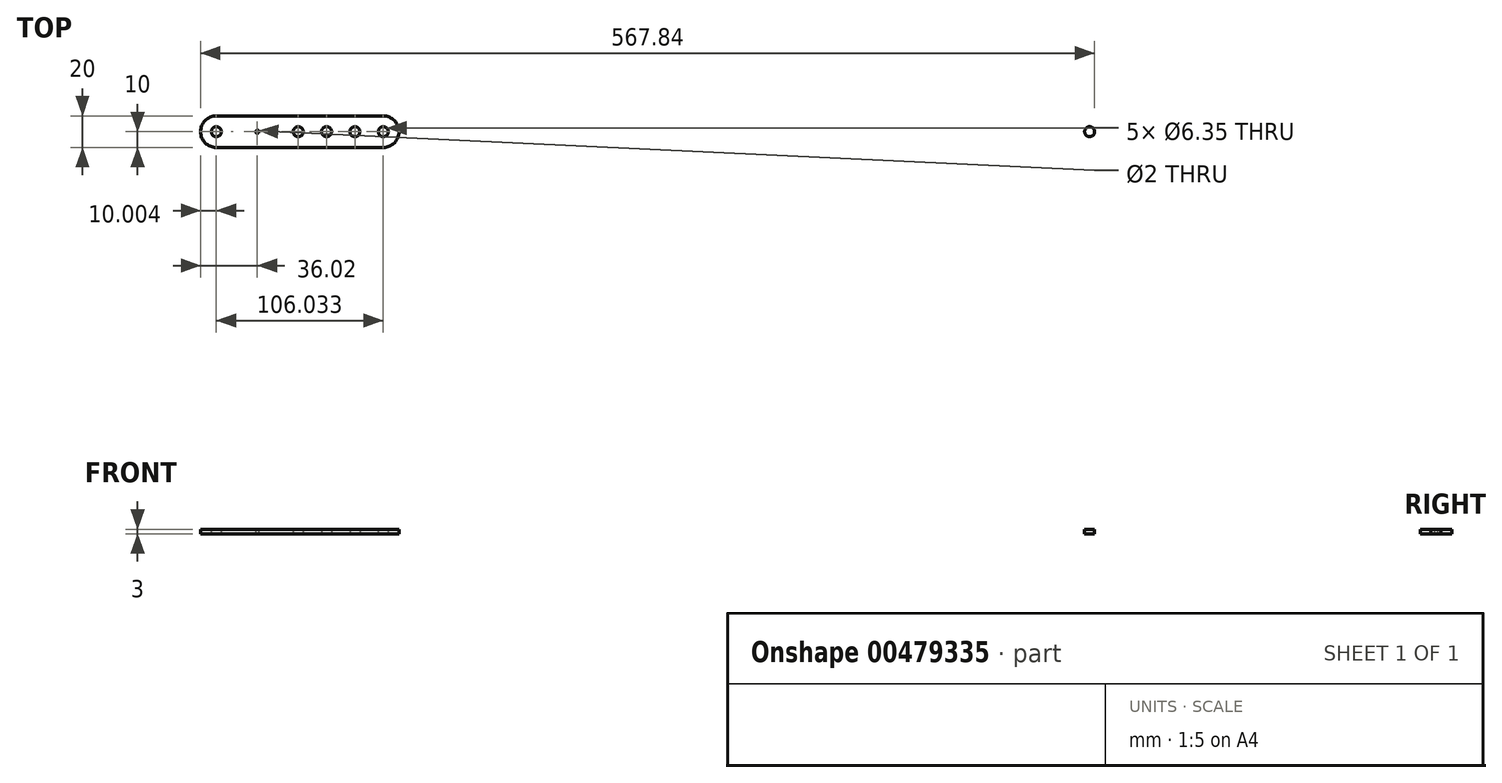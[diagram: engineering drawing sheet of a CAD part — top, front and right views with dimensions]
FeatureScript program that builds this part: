
annotation { "Feature Type Name" : "Feature", "Feature Type Description" : "" }
export const myFeature = defineFeature(function(context is Context, id is Id, definition is map)
    precondition{}
    {
        {
            var Q0;
            Q0=qCreatedBy(makeId("Top.planeOp"),FACE);
            var sketch = newSketch(context, id + "F0", { "sketchPlane" : qUnion([Q0])});
            skLineSegment(sketch, "E0", {"start": v(0, 0) * mm, "end": v(2599.19, 0) * mm, "construction": true});
            skCircle(sketch, "E1", {"center": v(528.65, 0) * mm, "radius": 3.18 * mm});
            skCircle(sketch, "E2", {"center": v(26.02, 0) * mm, "radius": 3.18 * mm});
            skCircle(sketch, "E3", {"center": v(0, 0) * mm, "radius": 13.8 * mm, "construction": true});
            skCircle(sketch, "E4.cCircle", {"center": v(26.02, 0) * mm, "radius": 6.35 * mm, "construction": true});
            skLineSegment(sketch, "E4.0", {"start": v(32.37, 0) * mm, "end": v(29.2, -5.5) * mm, "construction": true});
            skLineSegment(sketch, "E4.1", {"start": v(29.2, -5.5) * mm, "end": v(22.84, -5.5) * mm, "construction": true});
            skLineSegment(sketch, "E4.2", {"start": v(22.84, -5.5) * mm, "end": v(19.67, 0) * mm, "construction": true});
            skLineSegment(sketch, "E4.3", {"start": v(19.67, 0) * mm, "end": v(22.84, 5.5) * mm, "construction": true});
            skLineSegment(sketch, "E4.4", {"start": v(22.84, 5.5) * mm, "end": v(29.2, 5.5) * mm, "construction": true});
            skLineSegment(sketch, "E4.5", {"start": v(29.2, 5.5) * mm, "end": v(32.37, 0) * mm, "construction": true});
            skCircle(sketch, "E5.1.0.0", {"center": v(44.02, 0) * mm, "radius": 3.18 * mm});
            skCircle(sketch, "E5.1.0.1", {"center": v(44.02, 0) * mm, "radius": 6.35 * mm, "construction": true});
            skCircle(sketch, "E5.2.0.0", {"center": v(62.02, 0) * mm, "radius": 3.18 * mm});
            skCircle(sketch, "E5.2.0.1", {"center": v(62.02, 0) * mm, "radius": 6.35 * mm, "construction": true});
            skLineSegment(sketch, "E5.direction1", {"start": v(26.02, 0) * mm, "end": v(44.02, 0) * mm, "construction": true});
            skCircle(sketch, "E6.0.3.0", {"center": v(80.02, 0) * mm, "radius": 3.18 * mm});
            skCircle(sketch, "E6.2.3.0", {"center": v(80.02, 0) * mm, "radius": 6.35 * mm, "construction": true});
            skCircle(sketch, "E7", {"center": v(80.02, 0) * mm, "radius": 10 * mm});
            skCircle(sketch, "E8.MirrorC", {"center": v(-26.02, 0) * mm, "radius": 6.35 * mm, "construction": true});
            skCircle(sketch, "E9", {"center": v(-26.02, 0) * mm, "radius": 10 * mm});
            skLineSegment(sketch, "E10", {"start": v(-26.02, 10) * mm, "end": v(80.02, 10) * mm});
            skLineSegment(sketch, "E11.MirrorCS", {"start": v(-26.02, -10) * mm, "end": v(80.02, -10) * mm});
            skCircle(sketch, "E12", {"center": v(0, 0) * mm, "radius": 1 * mm});
            skCircle(sketch, "E13.MirrorC", {"center": v(-26.02, 0) * mm, "radius": 3.18 * mm});
            skSolve(sketch);
        }
        {
            var Q0;
            Q0 = qSketchRegion(id + "F0", true);
            extrude(context, id + "F1", {"entities" : qUnion([Q0]), "depth" : 3 * mm});
        }
    });
